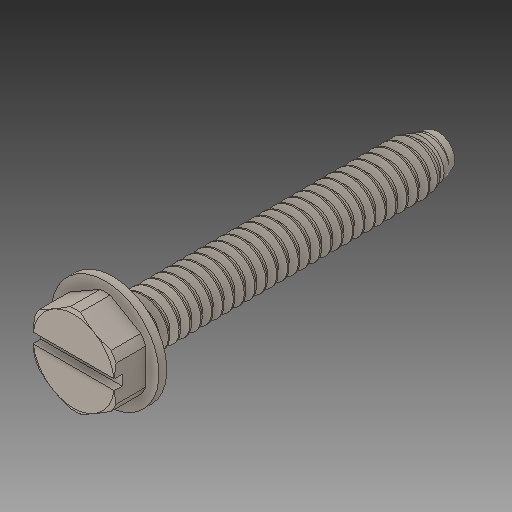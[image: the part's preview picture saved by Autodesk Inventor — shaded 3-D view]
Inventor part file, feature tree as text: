
AUTODESK INVENTOR PART (.ipt)
format: ipt  version: 2018 (Build 220112000, 112)  size: 1,202,688 bytes
history: native  units: in
note: dims shown in document units (in); Inventor stores cm internally (conversion verified against a paired STEP export)
features: extrude x1
ambient origin geometry x8: Origin, YZ Plane, XZ Plane, XY Plane, X Axis, Y Axis, Z Axis, Center Point
bodies: Solid1 (feature_tree)
feature tree (1):
  extrude  "Extrude4"  [1 undecoded]
note: 1 required parameter value undecoded (feature->parameter linkage not recoverable at this tier; creation-order binding heuristic only, values carry confidence <= 0.55)
